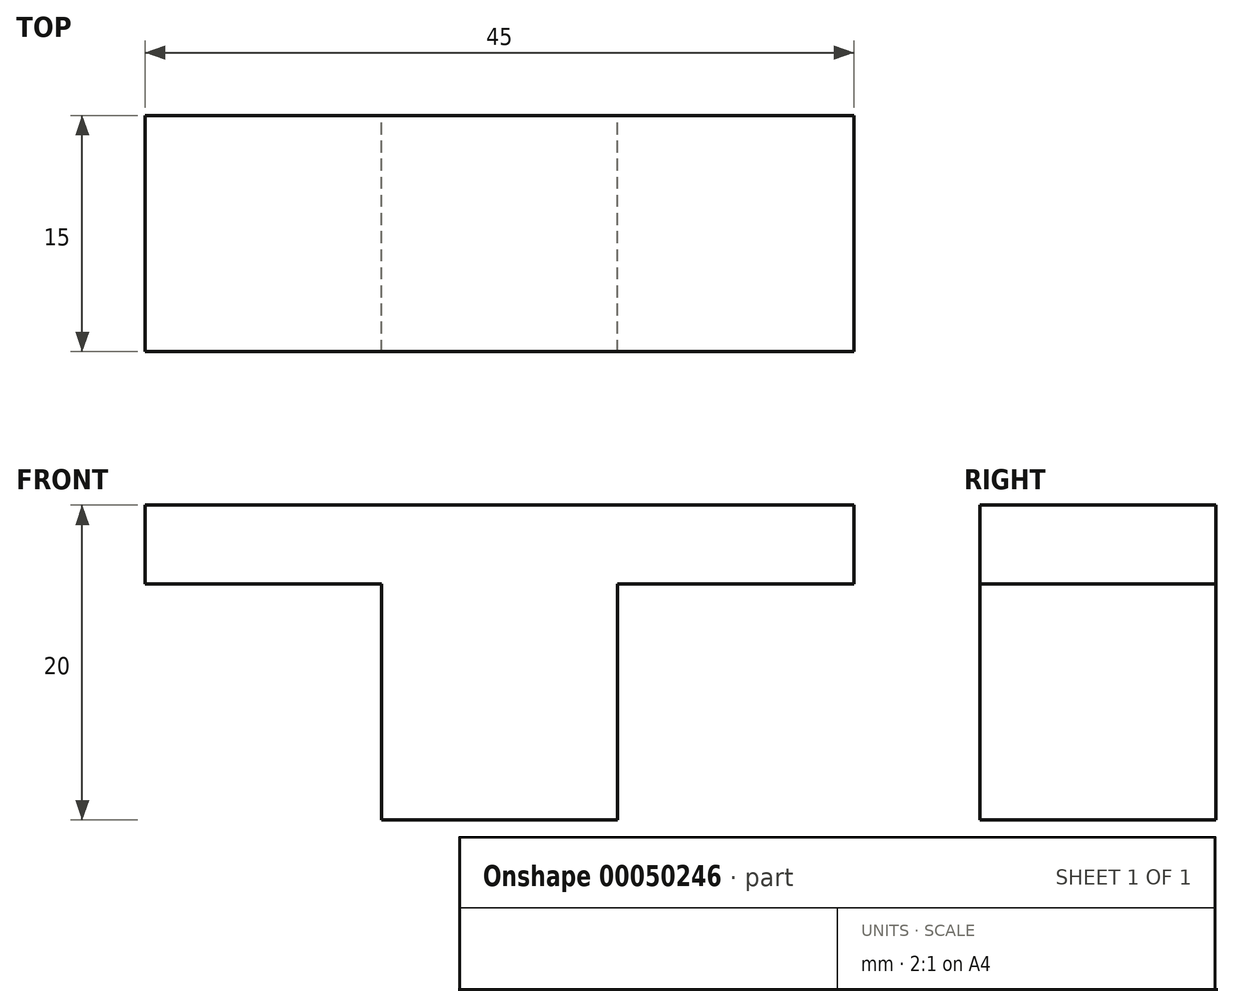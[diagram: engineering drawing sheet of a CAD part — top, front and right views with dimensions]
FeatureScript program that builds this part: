
annotation { "Feature Type Name" : "Feature", "Feature Type Description" : "" }
export const myFeature = defineFeature(function(context is Context, id is Id, definition is map)
    precondition{}
    {
        {
            var Q0;
            Q0=qCreatedBy(makeId("Front.planeOp"),FACE);
            var sketch = newSketch(context, id + "F0", { "sketchPlane" : qUnion([Q0])});
            skLineSegment(sketch, "E0.bottom", {"start": v(-22.5, 11.46) * mm, "end": v(22.5, 11.46) * mm});
            skLineSegment(sketch, "E0.top", {"start": v(-22.5, 6.46) * mm, "end": v(-7.5, 6.46) * mm});
            skLineSegment(sketch, "E0.left", {"start": v(-22.5, 11.46) * mm, "end": v(-22.5, 6.46) * mm});
            skLineSegment(sketch, "E0.right", {"start": v(22.5, 11.46) * mm, "end": v(22.5, 6.46) * mm});
            skLineSegment(sketch, "E1.top", {"start": v(-7.5, -8.54) * mm, "end": v(7.5, -8.54) * mm});
            skLineSegment(sketch, "E1.left", {"start": v(-7.5, 6.46) * mm, "end": v(-7.5, -8.54) * mm});
            skLineSegment(sketch, "E1.right", {"start": v(7.5, 6.46) * mm, "end": v(7.5, -8.54) * mm});
            skLineSegment(sketch, "E2.trimOffspring", {"start": v(7.5, 6.46) * mm, "end": v(22.5, 6.46) * mm});
            skSolve(sketch);
        }
        {
            var Q0;
            Q0 = qSketchRegion(id + "F0", true);
            extrude(context, id + "F1", {"entities" : qUnion([Q0]), "depth" : 15 * mm});
        }
    });
